# Revit family: 221010025038010
name_source: partatom
category: Generic Models
revit_build: Autodesk Revit 2018 (Build: 20190510_1515(x64)
units: mm (PartAtom-declared; Revit-internal decimal feet)

## family parameters
Always vertical = No
Can host rebar = No
Cut with Voids When Loaded = No
Part Type = Normal
Room Calculation Point = No
Round Connector Dimension = Use Diameter
Shared = No
Work Plane-Based = No

## types (1)
- PERNO CLIP ENCASTRE RAINBODECK NYLON N1C NATURAL
    Aplicacion = Perno requerido para la instalación de las tablas de Deck de WPC
    Color = Negro
    Description = PERNO CLIP ENCASTRE RAINBODECK NYLON N1C NATURAL
    Dimension = 0 mm  [stored 0 ft]
    Empresa = CNP SPA.
    Espesor = 0 mm  [stored 0 ft]
    Material = Cromado
    Model = PERNO CLIP ENCASTRE RAINBODECK
    Nombre SKU = PERNO CLIP ENCASTRE RAINBODECK NYLON N1C NATURAL
    Num SKUs = 221010025038010
    URL = https://www.empresascnp.cl
    Unidad = Por unidad.
    Url Ficha tecnica = https://empresascnp.cl

note: [stored X ft] marks values corroborated as IEEE doubles in the binary element streams (Revit-internal decimal feet)

## geometry (parser evidence)
native form markers: Sweep x2
no freeform markers — native parametric forms only
